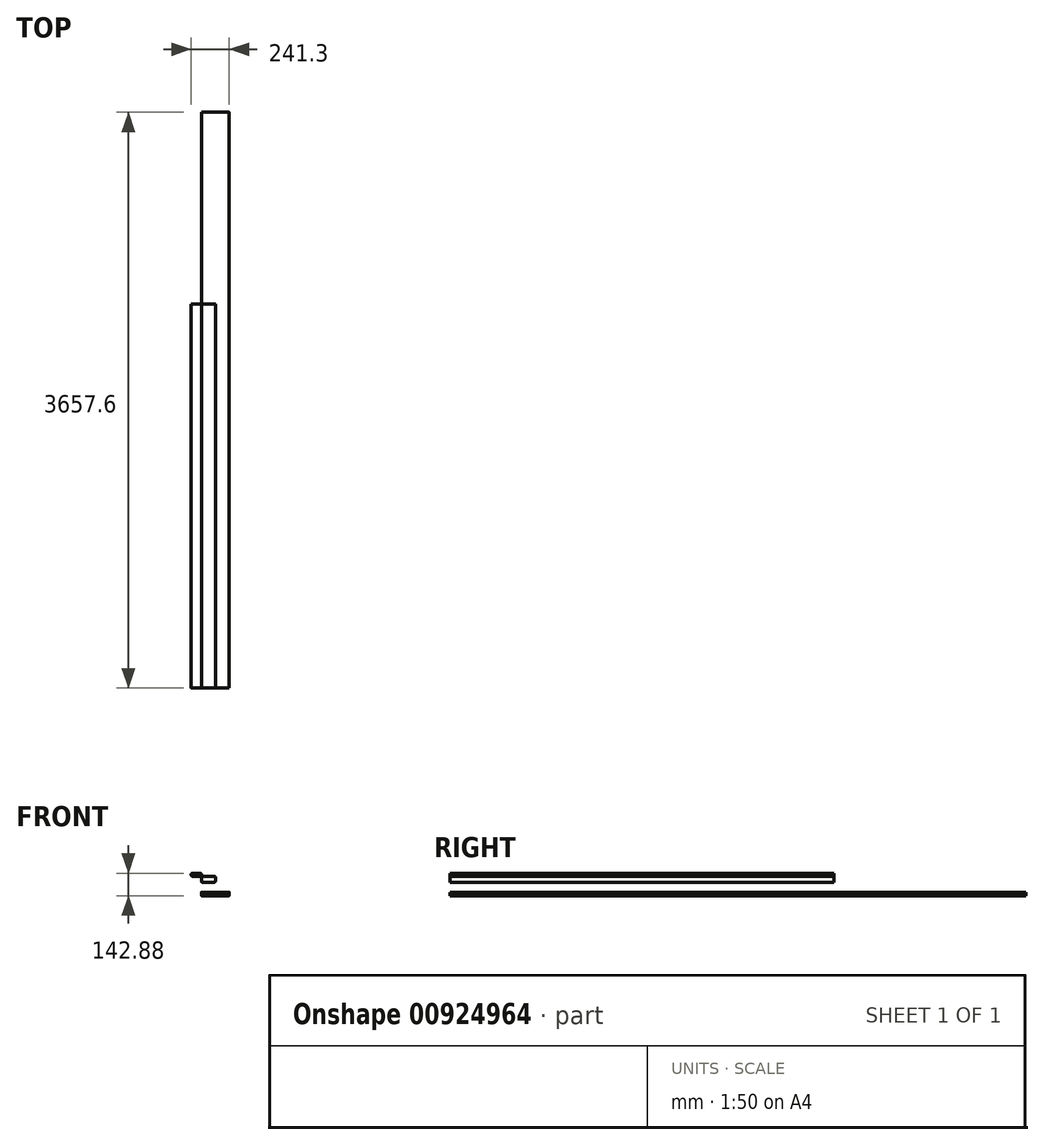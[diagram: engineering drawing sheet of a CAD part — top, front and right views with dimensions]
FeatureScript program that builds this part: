
annotation { "Feature Type Name" : "Feature", "Feature Type Description" : "" }
export const myFeature = defineFeature(function(context is Context, id is Id, definition is map)
    precondition{}
    {
        {
            var Q0;
            Q0=qCreatedBy(makeId("Front.planeOp"),FACE);
            var sketch = newSketch(context, id + "F0", { "sketchPlane" : qUnion([Q0])});
            skLineSegment(sketch, "E0.bottom", {"start": v(3.81, 0) * mm, "end": v(85.1, 0) * mm});
            skLineSegment(sketch, "E0.top", {"start": v(3.81, -38.1) * mm, "end": v(85.1, -38.1) * mm});
            skLineSegment(sketch, "E0.left", {"start": v(0, -3.81) * mm, "end": v(0, -34.3) * mm});
            skLineSegment(sketch, "E0.right", {"start": v(88.9, -3.81) * mm, "end": v(88.9, -34.3) * mm});
            skPoint(sketch, "E1.visualSharp", {"position": v(0, 0) * mm});
            skArc(sketch, "E1.filletArc", {"start": v(3.81, 0) * mm, "mid": v(1.12, -1.12) * mm, "end": v(0, -3.81) * mm});
            skPoint(sketch, "E2.visualSharp", {"position": v(0, -38.1) * mm});
            skArc(sketch, "E2.filletArc", {"start": v(0, -34.3) * mm, "mid": v(1.12, -36.98) * mm, "end": v(3.81, -38.1) * mm});
            skPoint(sketch, "E3.visualSharp", {"position": v(88.9, -38.1) * mm});
            skArc(sketch, "E3.filletArc", {"start": v(85.1, -38.1) * mm, "mid": v(87.78, -36.98) * mm, "end": v(88.9, -34.3) * mm});
            skPoint(sketch, "E4.visualSharp", {"position": v(88.9, 0) * mm});
            skArc(sketch, "E4.filletArc", {"start": v(88.9, -3.8) * mm, "mid": v(87.78, -1.12) * mm, "end": v(85.1, 0) * mm});
            skLineSegment(sketch, "E5.bottom", {"start": v(-3.81, 0) * mm, "end": v(-59.69, 0) * mm});
            skLineSegment(sketch, "E5.top", {"start": v(-3.81, 19.05) * mm, "end": v(-59.69, 19.05) * mm});
            skLineSegment(sketch, "E5.left", {"start": v(0, 3.81) * mm, "end": v(0, 15.24) * mm});
            skLineSegment(sketch, "E5.right", {"start": v(-63.5, 3.81) * mm, "end": v(-63.5, 15.24) * mm});
            skPoint(sketch, "E6.visualSharp", {"position": v(-63.5, 19.05) * mm});
            skArc(sketch, "E6.filletArc", {"start": v(-59.69, 19.05) * mm, "mid": v(-62.38, 17.93) * mm, "end": v(-63.5, 15.24) * mm});
            skPoint(sketch, "E7.visualSharp", {"position": v(-63.5, 0) * mm});
            skArc(sketch, "E7.filletArc", {"start": v(-63.5, 3.81) * mm, "mid": v(-62.38, 1.12) * mm, "end": v(-59.69, 0) * mm});
            skArc(sketch, "E8.filletArc", {"start": v(-3.81, 0) * mm, "mid": v(-1.12, 1.12) * mm, "end": v(0, 3.81) * mm});
            skPoint(sketch, "E9.visualSharp", {"position": v(0, 19.05) * mm});
            skArc(sketch, "E9.filletArc", {"start": v(0, 15.24) * mm, "mid": v(-1.12, 17.93) * mm, "end": v(-3.81, 19.05) * mm});
            skLineSegment(sketch, "E10.bottom", {"start": v(1.27, -101.6) * mm, "end": v(176.53, -101.6) * mm});
            skLineSegment(sketch, "E10.top", {"start": v(1.27, -123.83) * mm, "end": v(176.53, -123.83) * mm});
            skLineSegment(sketch, "E10.left", {"start": v(0, -102.87) * mm, "end": v(0, -122.56) * mm});
            skLineSegment(sketch, "E10.right", {"start": v(177.8, -102.87) * mm, "end": v(177.8, -122.56) * mm});
            skPoint(sketch, "E11.visualSharp", {"position": v(177.8, -101.6) * mm});
            skArc(sketch, "E11.filletArc", {"start": v(177.8, -102.87) * mm, "mid": v(177.43, -101.97) * mm, "end": v(176.53, -101.6) * mm});
            skPoint(sketch, "E12.visualSharp", {"position": v(177.8, -123.83) * mm});
            skArc(sketch, "E12.filletArc", {"start": v(176.53, -123.83) * mm, "mid": v(177.43, -123.45) * mm, "end": v(177.8, -122.56) * mm});
            skPoint(sketch, "E13.visualSharp", {"position": v(0, -123.83) * mm});
            skArc(sketch, "E13.filletArc", {"start": v(0, -122.56) * mm, "mid": v(0.37, -123.45) * mm, "end": v(1.27, -123.83) * mm});
            skPoint(sketch, "E14.visualSharp", {"position": v(0, -101.6) * mm});
            skArc(sketch, "E14.filletArc", {"start": v(1.27, -101.6) * mm, "mid": v(0.37, -101.97) * mm, "end": v(0, -102.87) * mm});
            skSolve(sketch);
        }
        {
            var Q0;
            Q0=makeQuery(id+"F0.imprint","IMPRINT",FACE,{"disambiguationData":[TD([[makeQuery(id+"F0.imprint","IMPRINT",EDGE,{"derivedFrom":sQuery(id+"F0.wireOp",EDGE,"E0.bottom")}),-1.0]])]});
            extrude(context, id + "F1", {"entities" : qUnion([Q0]), "oppositeDirection" : true, "depth" : 2438.4 * mm, "offsetDistance" : 25.4 * mm});
        }
        {
            var Q0;
            Q0=makeQuery(id+"F0.imprint","IMPRINT",FACE,{"disambiguationData":[TD([[makeQuery(id+"F0.imprint","IMPRINT",EDGE,{"derivedFrom":sQuery(id+"F0.wireOp",EDGE,"E5.bottom")}),-1.0]])]});
            extrude(context, id + "F2", {"entities" : qUnion([Q0]), "oppositeDirection" : true, "depth" : 2438.4 * mm, "offsetDistance" : 25.4 * mm});
        }
        {
            var Q0;
            Q0=makeQuery(id+"F0.imprint","IMPRINT",FACE,{"disambiguationData":[TD([[makeQuery(id+"F0.imprint","IMPRINT",EDGE,{"derivedFrom":sQuery(id+"F0.wireOp",EDGE,"E10.bottom")}),-1.0]])]});
            extrude(context, id + "F3", {"entities" : qUnion([Q0]), "oppositeDirection" : true, "depth" : 3657.6 * mm, "offsetDistance" : 25.4 * mm});
        }
    });
